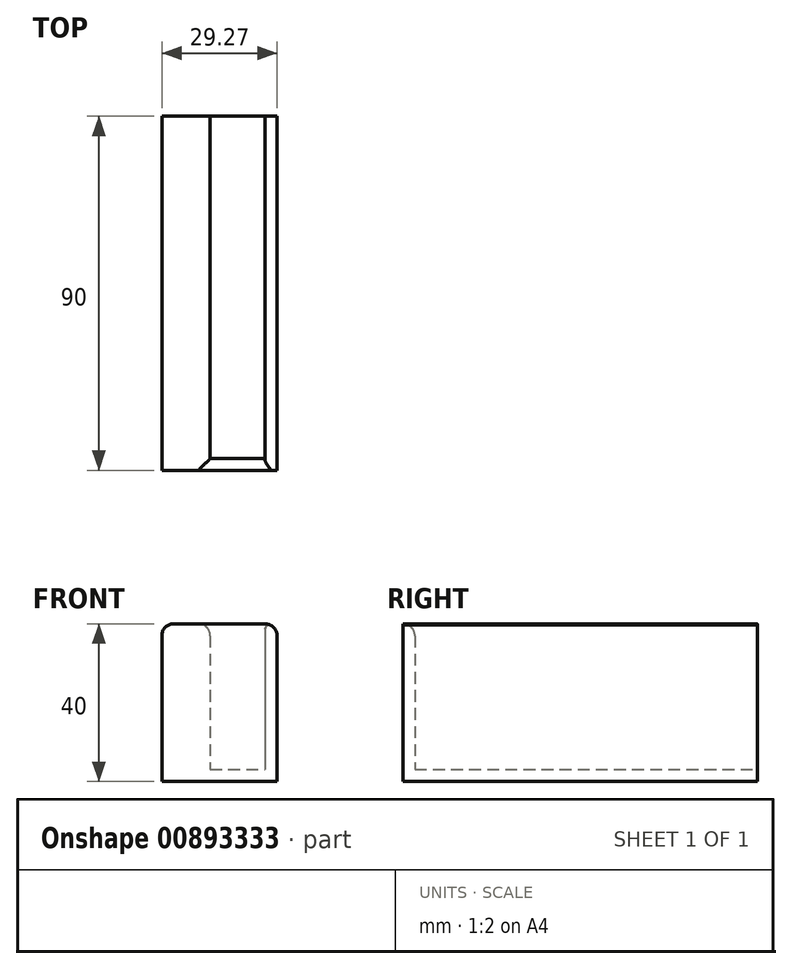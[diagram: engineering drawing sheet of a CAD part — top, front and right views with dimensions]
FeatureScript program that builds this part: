
annotation { "Feature Type Name" : "Feature", "Feature Type Description" : "" }
export const myFeature = defineFeature(function(context is Context, id is Id, definition is map)
    precondition{}
    {
        {
            var Q0;
            Q0=qCreatedBy(makeId("Top.planeOp"),FACE);
            var sketch = newSketch(context, id + "F0", { "sketchPlane" : qUnion([Q0])});
            skLineSegment(sketch, "E0.bottom", {"start": v(-17.07, 42.49) * mm, "end": v(-29.34, 42.49) * mm});
            skLineSegment(sketch, "E0.top", {"start": v(-17.07, -47.51) * mm, "end": v(-29.34, -47.51) * mm});
            skLineSegment(sketch, "E0.left", {"start": v(-17.07, 42.49) * mm, "end": v(-17.07, -47.51) * mm});
            skLineSegment(sketch, "E0.right", {"start": v(-29.34, 42.49) * mm, "end": v(-29.34, -47.51) * mm});
            skLineSegment(sketch, "E1.bottom", {"start": v(-17.07, -47.51) * mm, "end": v(-3.07, -47.51) * mm});
            skLineSegment(sketch, "E1.top", {"start": v(-17.07, -44.51) * mm, "end": v(-3.07, -44.51) * mm});
            skLineSegment(sketch, "E1.left", {"start": v(-17.07, -47.51) * mm, "end": v(-17.07, -44.51) * mm});
            skLineSegment(sketch, "E1.right", {"start": v(-3.07, -47.51) * mm, "end": v(-3.07, -44.51) * mm});
            skLineSegment(sketch, "E2.bottom", {"start": v(-3.07, -47.51) * mm, "end": v(-3.07, -47.51) * mm});
            skLineSegment(sketch, "E2.top", {"start": v(-3.07, -47.51) * mm, "end": v(-3.07, -47.51) * mm});
            skLineSegment(sketch, "E2.left", {"start": v(-3.07, -47.51) * mm, "end": v(-3.07, -47.51) * mm});
            skLineSegment(sketch, "E2.right", {"start": v(-3.07, -47.51) * mm, "end": v(-3.07, -47.51) * mm});
            skLineSegment(sketch, "E3.bottom", {"start": v(-3.07, -47.51) * mm, "end": v(-0.07, -47.51) * mm});
            skLineSegment(sketch, "E3.top", {"start": v(-3.07, 42.49) * mm, "end": v(-0.07, 42.49) * mm});
            skLineSegment(sketch, "E3.left", {"start": v(-3.07, -47.51) * mm, "end": v(-3.07, 42.49) * mm});
            skLineSegment(sketch, "E3.right", {"start": v(-0.07, -47.51) * mm, "end": v(-0.07, 42.49) * mm});
            skSolve(sketch);
        }
        {
            var Q0;
            Q0 = qSketchRegion(id + "F0", true);
            extrude(context, id + "F1", {"entities" : qUnion([Q0]), "depth" : 37 * mm, "offsetDistance" : 25 * mm});
        }
        {
            var Q0;
            Q0=qCreatedBy(makeId("Top.planeOp"),FACE);
            var sketch = newSketch(context, id + "F2", { "sketchPlane" : qUnion([Q0])});
            skLineSegment(sketch, "E4.0", {"start": v(-29.34, 42.49) * mm, "end": v(-29.34, -47.51) * mm});
            skLineSegment(sketch, "E5.0", {"start": v(-0.07, -47.51) * mm, "end": v(-0.07, 42.49) * mm});
            skLineSegment(sketch, "E6.0", {"start": v(-17.07, -47.51) * mm, "end": v(-29.34, -47.51) * mm});
            skLineSegment(sketch, "E7.0", {"start": v(-17.07, 42.49) * mm, "end": v(-29.34, 42.49) * mm});
            skLineSegment(sketch, "E8.0", {"start": v(-3.07, 42.49) * mm, "end": v(-0.07, 42.49) * mm});
            skLineSegment(sketch, "E9.0", {"start": v(-3.07, -47.51) * mm, "end": v(-0.07, -47.51) * mm});
            skLineSegment(sketch, "E10.bottom", {"start": v(-29.34, -47.51) * mm, "end": v(-0.07, -47.51) * mm});
            skLineSegment(sketch, "E10.top", {"start": v(-29.34, 42.49) * mm, "end": v(-0.07, 42.49) * mm});
            skLineSegment(sketch, "E10.left", {"start": v(-29.34, -47.51) * mm, "end": v(-29.34, 42.49) * mm});
            skSolve(sketch);
        }
        {
            var Q0;
            Q0 = qSketchRegion(id + "F2", true);
            extrude(context, id + "F3", {"entities" : qUnion([Q0]), "operationType" : NewBodyOperationType.ADD, "oppositeDirection" : true, "depth" : 3 * mm, "offsetDistance" : 25 * mm});
        }
        {
            var Q0;
            Q0=makeQuery(id+"F1.opExtrude","CAP_EDGE",EDGE,{"disambiguationData":[OSD([sQuery(id+"F0.wireOp",EDGE,"E3.right")])],"isStart":false});
            fillet(context, id + "F4", {"entities" : qUnion([Q0]), "radius" : 3 * mm, "tangentPropagation" : true, "allowEdgeOverflow" : false});
        }
        {
            var Q0;
            Q0=makeQuery(id+"F1.opExtrude","CAP_EDGE",EDGE,{"disambiguationData":[OSD([sQuery(id+"F0.wireOp",EDGE,"E0.right")])],"isStart":false});
            fillet(context, id + "F5", {"entities" : qUnion([Q0]), "radius" : 3 * mm, "tangentPropagation" : true, "allowEdgeOverflow" : false});
        }
        {
            var Q0;
            Q0=makeQuery(id+"F1.opExtrude","CAP_EDGE",EDGE,{"disambiguationData":[OSD([sQuery(id+"F0.wireOp",EDGE,"E0.left")])],"isStart":false});
            fillet(context, id + "F6", {"entities" : qUnion([Q0]), "radius" : 3 * mm, "tangentPropagation" : true, "allowEdgeOverflow" : false});
        }
        {
            var Q0;
            Q0=makeQuery(id+"F4.opFillet","BLEND_EDGE",EDGE,{"blendedFrom":[makeQuery(id+"F1.opExtrude","CAP_EDGE",EDGE,{"disambiguationData":[OSD([sQuery(id+"F0.wireOp",EDGE,"E3.right")])],"isStart":false}),makeQuery(id+"F1.opExtrude","SWEPT_FACE",FACE,{"disambiguationData":[OSD([sQuery(id+"F0.wireOp",EDGE,"E3.left")])]})],"blendedInto":[makeQuery(id+"F1.opExtrude","SWEPT_FACE",FACE,{"disambiguationData":[OSD([sQuery(id+"F0.wireOp",EDGE,"E3.left")])]})]});
            fillet(context, id + "F7", {"entities" : qUnion([Q0]), "radius" : 1 * mm, "tangentPropagation" : true, "allowEdgeOverflow" : false});
        }
        {
            var Q0;
            Q0=makeQuery(id+"F1.opExtrude","CAP_EDGE",EDGE,{"disambiguationData":[OSD([sQuery(id+"F0.wireOp",EDGE,"E1.top")])],"isStart":false});
            fillet(context, id + "F8", {"entities" : qUnion([Q0]), "radius" : 3 * mm, "tangentPropagation" : true, "allowEdgeOverflow" : false});
        }
    });
